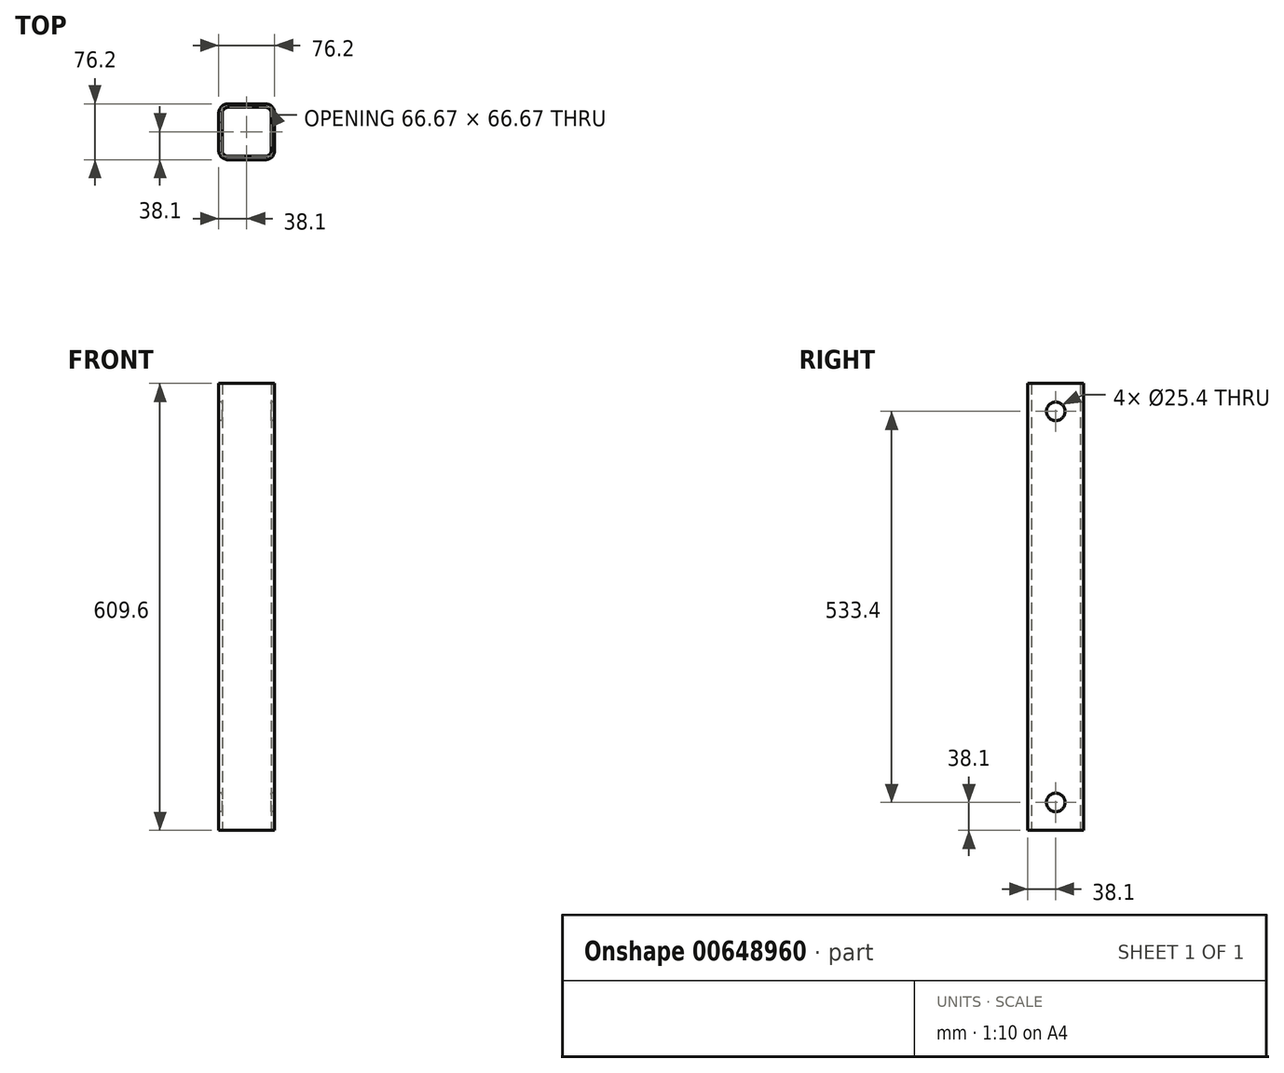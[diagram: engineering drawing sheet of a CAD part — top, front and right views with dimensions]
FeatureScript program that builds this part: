
annotation { "Feature Type Name" : "Feature", "Feature Type Description" : "" }
export const myFeature = defineFeature(function(context is Context, id is Id, definition is map)
    precondition{}
    {
        {
            var Q0;
            Q0=qCreatedBy(makeId("Top.planeOp"),FACE);
            var sketch = newSketch(context, id + "F0", { "sketchPlane" : qUnion([Q0])});
            skLineSegment(sketch, "E0.bottom", {"start": v(25.4, 38.1) * mm, "end": v(-25.4, 38.1) * mm});
            skLineSegment(sketch, "E0.top", {"start": v(25.4, -38.1) * mm, "end": v(-25.4, -38.1) * mm});
            skLineSegment(sketch, "E0.left", {"start": v(38.1, 25.4) * mm, "end": v(38.1, -25.4) * mm});
            skLineSegment(sketch, "E0.right", {"start": v(-38.1, 25.4) * mm, "end": v(-38.1, -25.4) * mm});
            skPoint(sketch, "E0.middle", {"position": v(0, 0) * mm});
            skPoint(sketch, "E1.visualSharp", {"position": v(38.1, 38.1) * mm});
            skArc(sketch, "E1.filletArc", {"start": v(38.1, 25.4) * mm, "mid": v(34.38, 34.38) * mm, "end": v(25.4, 38.1) * mm});
            skPoint(sketch, "E2.visualSharp", {"position": v(-38.1, 38.1) * mm});
            skArc(sketch, "E2.filletArc", {"start": v(-25.4, 38.1) * mm, "mid": v(-34.38, 34.38) * mm, "end": v(-38.1, 25.4) * mm});
            skPoint(sketch, "E3.visualSharp", {"position": v(-38.1, -38.1) * mm});
            skArc(sketch, "E3.filletArc", {"start": v(-38.1, -25.4) * mm, "mid": v(-34.38, -34.38) * mm, "end": v(-25.4, -38.1) * mm});
            skPoint(sketch, "E4.visualSharp", {"position": v(38.1, -38.1) * mm});
            skArc(sketch, "E4.filletArc", {"start": v(25.4, -38.1) * mm, "mid": v(34.38, -34.38) * mm, "end": v(38.1, -25.4) * mm});
            skArc(sketch, "E5.0", {"start": v(33.34, 25.4) * mm, "mid": v(31.01, 31.01) * mm, "end": v(25.4, 33.34) * mm});
            skLineSegment(sketch, "E5.1", {"start": v(33.34, 25.4) * mm, "end": v(33.34, -25.4) * mm});
            skLineSegment(sketch, "E5.2", {"start": v(25.4, 33.34) * mm, "end": v(-25.4, 33.34) * mm});
            skArc(sketch, "E5.3", {"start": v(25.4, -33.34) * mm, "mid": v(31.01, -31.01) * mm, "end": v(33.34, -25.4) * mm});
            skArc(sketch, "E5.4", {"start": v(-25.4, 33.34) * mm, "mid": v(-31.01, 31.01) * mm, "end": v(-33.34, 25.4) * mm});
            skLineSegment(sketch, "E5.5", {"start": v(-33.34, 25.4) * mm, "end": v(-33.34, -25.4) * mm});
            skArc(sketch, "E5.6", {"start": v(-33.34, -25.4) * mm, "mid": v(-31.01, -31.01) * mm, "end": v(-25.4, -33.34) * mm});
            skLineSegment(sketch, "E5.7", {"start": v(25.4, -33.34) * mm, "end": v(-25.4, -33.34) * mm});
            skSolve(sketch);
        }
        {
            var Q0;
            Q0=qSketchRegion(id+"F0",true);
            extrude(context, id + "F1", {"entities" : qUnion([Q0]), "depth" : 609.6 * mm, "offsetDistance" : 25.4 * mm});
        }
        {
            var Q0;
            Q0=makeQuery(id+"F1.opExtrude","SWEPT_FACE",FACE,{"disambiguationData":[OSD([sQuery(id+"F0.wireOp",EDGE,"E0.left")])]});
            var sketch = newSketch(context, id + "F2", { "sketchPlane" : qUnion([Q0])});
            skLineSegment(sketch, "E6", {"start": v(0, 609.6) * mm, "end": v(0, 571.5) * mm});
            skLineSegment(sketch, "E7", {"start": v(0, 38.1) * mm, "end": v(0, 0) * mm});
            skSolve(sketch);
        }
        {
            var Q0;
            Q0=sQuery(id+"F2.wireOp",VERTEX,"E6.end");
            var Q1;
            Q1=sQuery(id+"F2.wireOp",VERTEX,"E7.start");
            var Q2;
            Q2=makeQuery(id+"F1.opExtrude","SWEPT_BODY",BODY,{"disambiguationData":[OSD([sQuery(id+"F0.wireOp",EDGE,"E0.bottom"),sQuery(id+"F0.wireOp",EDGE,"E0.top"),sQuery(id+"F0.wireOp",EDGE,"E0.left"),sQuery(id+"F0.wireOp",EDGE,"E0.right"),sQuery(id+"F0.wireOp",EDGE,"E1.filletArc"),sQuery(id+"F0.wireOp",EDGE,"E2.filletArc"),sQuery(id+"F0.wireOp",EDGE,"E3.filletArc"),sQuery(id+"F0.wireOp",EDGE,"E4.filletArc"),sQuery(id+"F0.wireOp",EDGE,"E5.0"),sQuery(id+"F0.wireOp",EDGE,"E5.1"),sQuery(id+"F0.wireOp",EDGE,"E5.2"),sQuery(id+"F0.wireOp",EDGE,"E5.3"),sQuery(id+"F0.wireOp",EDGE,"E5.4"),sQuery(id+"F0.wireOp",EDGE,"E5.5"),sQuery(id+"F0.wireOp",EDGE,"E5.6"),sQuery(id+"F0.wireOp",EDGE,"E5.7")])]});
            hole(context, id + "F3", {"style" : HoleStyle.SIMPLE, "endStyle" : HoleEndStyle.THROUGH, "holeDiameter" : 25.4 * mm, "majorDiameter" : 6.35 * mm, "isTappedThrough" : true, "tappedDepth" : 12.7 * mm, "tapClearance" : 3, "locations" : qUnion([Q0, Q1]), "scope" : qUnion([Q2])});
        }
    });
